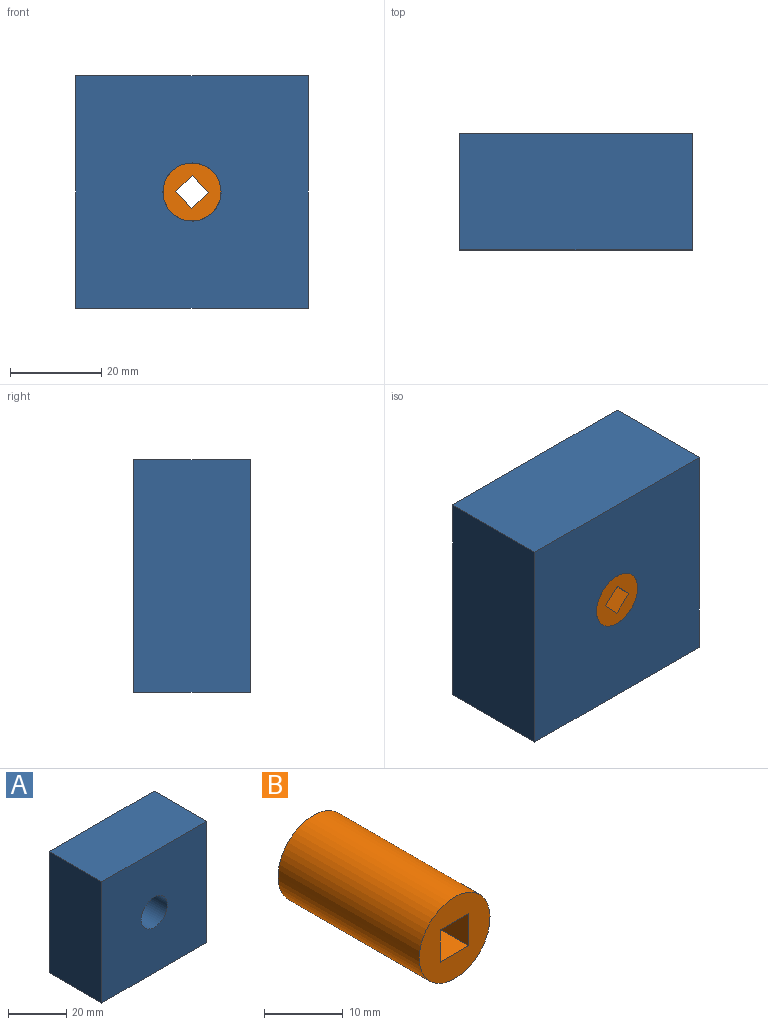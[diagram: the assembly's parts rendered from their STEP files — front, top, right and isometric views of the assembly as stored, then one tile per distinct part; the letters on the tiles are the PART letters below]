
ASSEMBLY  parts=2 mates=1
PART A: 7 faces, bbox 50.8x25.4x50.8 mm
  f0: plane 50.8x25.4mm, normal (0,0,-1), area 1290.3mm2, adj f1,f4,f5,f6
  f1: plane 50.8x25.4mm, normal (1,0,0), area 1290.3mm2, adj f0,f2,f5,f6
  f2: plane 50.8x25.4mm, normal (0,0,1), area 1290.3mm2, adj f1,f4,f5,f6
  f3: cylinder r=6.35mm len=25.4mm, axis (0,1,0), area 1013.4mm2, adj f5,f6
  f4: plane 50.8x25.4mm, normal (-1,0,0), area 1290.3mm2, adj f0,f2,f5,f6
  f5: plane 50.8x50.8mm, normal (0,-1,0), area 2454mm2, adj f0,f1,f2,f3,f4
  f6: plane 50.8x50.8mm, normal (0,1,0), area 2454mm2, adj f0,f1,f2,f3,f4
PART B: 7 faces, bbox 12.7x25.4x12.7 mm
  f0: plane 12.7x12.7mm, normal (0,-1,0), area 101.1mm2, adj f2,f3,f4,f5,f6
  f1: plane 12.7x12.7mm, normal (0,1,0), area 101.1mm2, adj f2,f3,f4,f5,f6
  f2: cylinder r=6.35mm len=25.4mm, axis (0,1,0), area 1013.4mm2, adj f0,f1
  f3: plane 25.4x5.11mm, normal (0,0,1), area 129.9mm2, adj f0,f1,f4,f6
  f4: plane 25.4x5mm, normal (-1,0,0), area 127mm2, adj f0,f1,f3,f5
  f5: plane 25.4x5.11mm, normal (0,0,-1), area 129.9mm2, adj f0,f1,f4,f6
  f6: plane 25.4x5mm, normal (1,0,0), area 127mm2, adj f0,f1,f3,f5
PLACE A at identity fixed
PLACE B rot(axis=(0,1,0),46.6deg) t=(0,0,0)mm
MATE revolute B.f2 <-> A.f3  axis (0,1,0) through (0,-25.4,0)mm
